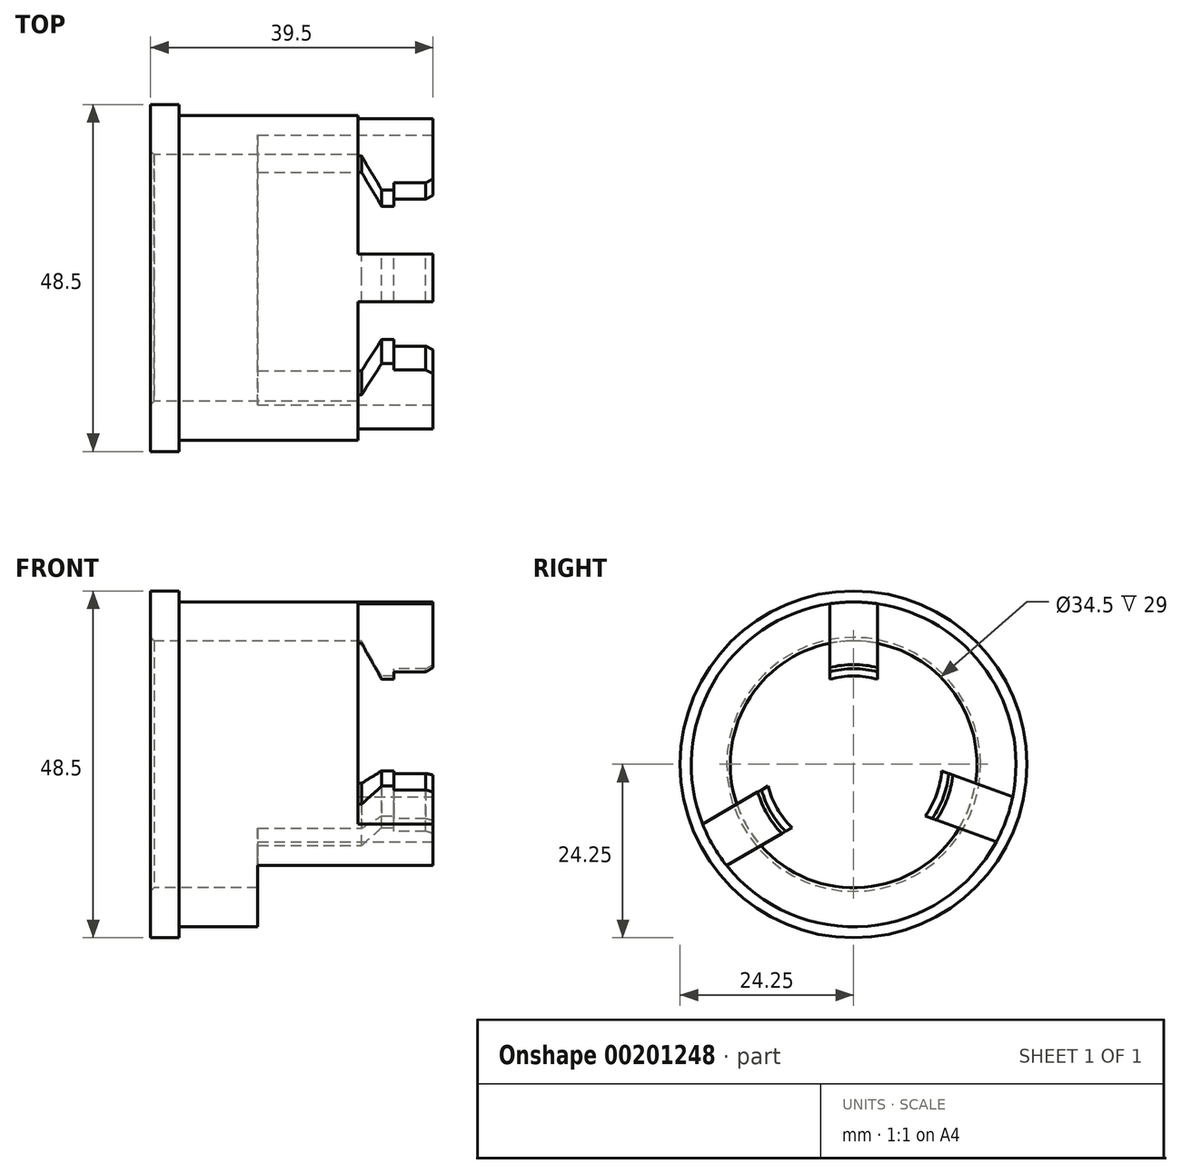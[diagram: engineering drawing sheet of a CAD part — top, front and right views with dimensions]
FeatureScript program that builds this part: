
annotation { "Feature Type Name" : "Feature", "Feature Type Description" : "" }
export const myFeature = defineFeature(function(context is Context, id is Id, definition is map)
    precondition{}
    {
        {
            var Q0;
            Q0=qCreatedBy(makeId("Front.planeOp"),FACE);
            var sketch = newSketch(context, id + "F0", { "sketchPlane" : qUnion([Q0])});
            skLineSegment(sketch, "E0", {"start": v(-7.14, 0) * mm, "end": v(50.19, 0) * mm, "construction": true});
            skLineSegment(sketch, "E1", {"start": v(0, 17.75) * mm, "end": v(0, 24.25) * mm});
            skLineSegment(sketch, "E2", {"start": v(0, 24.25) * mm, "end": v(4, 24.25) * mm});
            skLineSegment(sketch, "E3", {"start": v(4, 24.25) * mm, "end": v(4, 22.7) * mm});
            skLineSegment(sketch, "E4", {"start": v(4, 22.7) * mm, "end": v(39.5, 22.7) * mm});
            skLineSegment(sketch, "E5", {"start": v(39.5, 22.7) * mm, "end": v(39.5, 13.94) * mm});
            skLineSegment(sketch, "E6", {"start": v(39.5, 13.94) * mm, "end": v(38.5, 13.36) * mm});
            skLineSegment(sketch, "E7", {"start": v(38.5, 13.36) * mm, "end": v(34, 13.36) * mm});
            skLineSegment(sketch, "E8", {"start": v(34, 13.36) * mm, "end": v(34, 12.35) * mm});
            skLineSegment(sketch, "E9", {"start": v(34, 12.35) * mm, "end": v(32.33, 12.35) * mm});
            skLineSegment(sketch, "E10", {"start": v(32.33, 12.35) * mm, "end": v(29.5, 17.25) * mm});
            skLineSegment(sketch, "E11", {"start": v(29.5, 17.25) * mm, "end": v(0.5, 17.25) * mm});
            skLineSegment(sketch, "E12", {"start": v(0, 17.75) * mm, "end": v(0.5, 17.25) * mm});
            skSolve(sketch);
        }
        {
            var Q0;
            Q0=makeQuery(id+"F0.imprint","IMPRINT",FACE,{"disambiguationData":[TD([[makeQuery(id+"F0.imprint","IMPRINT",EDGE,{"derivedFrom":sQuery(id+"F0.wireOp",EDGE,"E1")}),-1.0]])]});
            var Q1;
            Q1=sQuery(id+"F0.wireOp",EDGE,"E0");
            revolve(context, id + "F1", {"entities" : qUnion([Q0]), "axis" : qUnion([Q1]), "revolveType" : RevolveType.FULL});
        }
        {
            var Q0;
            Q0=makeQuery(id+"F1.opRevolve","SWEPT_FACE",FACE,{"disambiguationData":[OSD([sQuery(id+"F0.wireOp",EDGE,"E5")])]});
            var sketch = newSketch(context, id + "F2", { "sketchPlane" : qUnion([Q0])});
            skLineSegment(sketch, "E13", {"start": v(0, 25.1) * mm, "end": v(0, -24.92) * mm, "construction": true});
            skLineSegment(sketch, "E14", {"start": v(-25.58, 0) * mm, "end": v(25.16, 0) * mm, "construction": true});
            skLineSegment(sketch, "E15", {"start": v(-3.35, 22.45) * mm, "end": v(-3.35, 11.89) * mm});
            skLineSegment(sketch, "E16", {"start": v(3.35, 22.45) * mm, "end": v(3.35, 11.89) * mm});
            skLineSegment(sketch, "E17", {"start": v(12.32, -0.92) * mm, "end": v(22.24, -4.53) * mm});
            skLineSegment(sketch, "E18", {"start": v(13.1, -4.77) * mm, "end": v(21.33, -7.76) * mm, "construction": true});
            skLineSegment(sketch, "E19", {"start": v(10.02, -7.21) * mm, "end": v(19.95, -10.83) * mm});
            skLineSegment(sketch, "E20", {"start": v(-19.66, -11.35) * mm, "end": v(-12.07, -6.97) * mm, "construction": true});
            skLineSegment(sketch, "E21", {"start": v(-21.12, -8.32) * mm, "end": v(-11.97, -3.04) * mm});
            skLineSegment(sketch, "E22", {"start": v(-17.77, -14.13) * mm, "end": v(-8.62, -8.84) * mm});
            skCircle(sketch, "E23.0", {"center": v(0, 0) * mm, "radius": 13.36 * mm});
            skCircle(sketch, "E24.0", {"center": v(0, 0) * mm, "radius": 12.35 * mm});
            skArc(sketch, "E25", {"start": v(-3.35, 16.92) * mm, "mid": v(-14.94, 8.62) * mm, "end": v(-16.33, -5.56) * mm});
            skArc(sketch, "E26.trimOffspring", {"start": v(17.05, -2.64) * mm, "mid": v(14.13, 9.9) * mm, "end": v(3.35, 16.92) * mm});
            skArc(sketch, "E27.trimOffspring", {"start": v(-12.98, -11.36) * mm, "mid": v(1.5, -17.18) * mm, "end": v(14.76, -8.94) * mm});
            skSolve(sketch);
        }
        {
            var Q0;
            {var subQ3=sQuery(id+"F2.wireOp",EDGE,"E25");Q0=makeQuery(id+"F2.imprint","IMPRINT",FACE,{"disambiguationData":[TD([[makeQuery(id+"F2.imprint","IMPRINT",EDGE,{"derivedFrom":subQ3}),-1.0]])]});}
            var Q1;
            {var subQ3=sQuery(id+"F2.wireOp",EDGE,"E26.trimOffspring");Q1=makeQuery(id+"F2.imprint","IMPRINT",FACE,{"disambiguationData":[TD([[makeQuery(id+"F2.imprint","IMPRINT",EDGE,{"derivedFrom":subQ3}),-1.0]])]});}
            extrude(context, id + "F3", {"entities" : qUnion([Q0, Q1]), "operationType" : NewBodyOperationType.REMOVE, "oppositeDirection" : true, "depth" : 10.5 * mm});
        }
        {
            var Q0;
            {var subQ0=sQuery(id+"F2.wireOp",EDGE,"E25");Q0=makeQuery(id+"F2.imprint","IMPRINT",FACE,{"disambiguationData":[TD([[makeQuery(id+"F2.imprint","IMPRINT",EDGE,{"derivedFrom":subQ0}),1.0]])]});}
            var Q1;
            {var subQ0=sQuery(id+"F2.wireOp",EDGE,"E26.trimOffspring");Q1=makeQuery(id+"F2.imprint","IMPRINT",FACE,{"disambiguationData":[TD([[makeQuery(id+"F2.imprint","IMPRINT",EDGE,{"derivedFrom":subQ0}),1.0]])]});}
            var Q2;
            {var subQ0=sQuery(id+"F2.wireOp",EDGE,"E24.0");var subQ1=sQuery(id+"F2.wireOp",EDGE,"E15");var subQ2=makeQuery(id+"F2.imprint","INTERSECT",VERTEX,{"derivedFrom":[subQ1,subQ0]});Q2=makeQuery(id+"F2.imprint","IMPRINT",FACE,{"disambiguationData":[TD([[makeQuery(id+"F2.imprint","IMPRINT",EDGE,{"disambiguationData":[TD([[subQ2,1.0]])],"derivedFrom":subQ1}),-1.0]])]});}
            var Q3;
            {var subQ0=sQuery(id+"F2.wireOp",EDGE,"E23.0");var subQ1=sQuery(id+"F2.wireOp",EDGE,"E15");var subQ2=makeQuery(id+"F2.imprint","INTERSECT",VERTEX,{"derivedFrom":[subQ1,subQ0]});Q3=makeQuery(id+"F2.imprint","IMPRINT",FACE,{"disambiguationData":[TD([[makeQuery(id+"F2.imprint","IMPRINT",EDGE,{"disambiguationData":[TD([[subQ2,-1.0]])],"derivedFrom":subQ0}),-1.0]])]});}
            var Q4;
            {var subQ0=sQuery(id+"F2.wireOp",EDGE,"E24.0");var subQ1=sQuery(id+"F2.wireOp",EDGE,"E16");var subQ2=makeQuery(id+"F2.imprint","INTERSECT",VERTEX,{"derivedFrom":[subQ1,subQ0]});Q4=makeQuery(id+"F2.imprint","IMPRINT",FACE,{"disambiguationData":[TD([[makeQuery(id+"F2.imprint","IMPRINT",EDGE,{"disambiguationData":[TD([[subQ2,1.0]])],"derivedFrom":subQ1}),1.0]])]});}
            var Q5;
            {var subQ0=sQuery(id+"F2.wireOp",EDGE,"E23.0");var subQ1=sQuery(id+"F2.wireOp",EDGE,"E16");var subQ2=makeQuery(id+"F2.imprint","INTERSECT",VERTEX,{"derivedFrom":[subQ1,subQ0]});Q5=makeQuery(id+"F2.imprint","IMPRINT",FACE,{"disambiguationData":[TD([[makeQuery(id+"F2.imprint","IMPRINT",EDGE,{"disambiguationData":[TD([[subQ2,1.0]])],"derivedFrom":subQ0}),-1.0]])]});}
            extrude(context, id + "F4", {"entities" : qUnion([Q0, Q1, Q2, Q3, Q4, Q5]), "operationType" : NewBodyOperationType.REMOVE, "endBound" : BoundingType.THROUGH_ALL, "oppositeDirection" : true, "depth" : 25 * mm});
        }
        {
            var Q0;
            {var subQ3=sQuery(id+"F2.wireOp",EDGE,"E27.trimOffspring");Q0=makeQuery(id+"F2.imprint","IMPRINT",FACE,{"disambiguationData":[TD([[makeQuery(id+"F2.imprint","IMPRINT",EDGE,{"derivedFrom":subQ3}),-1.0]])]});}
            extrude(context, id + "F5", {"entities" : qUnion([Q0]), "operationType" : NewBodyOperationType.REMOVE, "oppositeDirection" : true, "depth" : 24.5 * mm});
        }
        {
            var Q0;
            {var subQ0=sQuery(id+"F2.wireOp",EDGE,"E27.trimOffspring");Q0=makeQuery(id+"F2.imprint","IMPRINT",FACE,{"disambiguationData":[TD([[makeQuery(id+"F2.imprint","IMPRINT",EDGE,{"derivedFrom":subQ0}),1.0]])]});}
            var Q1;
            {var subQ0=sQuery(id+"F2.wireOp",EDGE,"E24.0");var subQ1=sQuery(id+"F2.wireOp",EDGE,"E19");var subQ2=makeQuery(id+"F2.imprint","INTERSECT",VERTEX,{"derivedFrom":[subQ1,subQ0]});Q1=makeQuery(id+"F2.imprint","IMPRINT",FACE,{"disambiguationData":[TD([[makeQuery(id+"F2.imprint","IMPRINT",EDGE,{"disambiguationData":[TD([[subQ2,-1.0]])],"derivedFrom":subQ1}),-1.0]])]});}
            var Q2;
            {var subQ0=sQuery(id+"F2.wireOp",EDGE,"E23.0");var subQ1=sQuery(id+"F2.wireOp",EDGE,"E19");var subQ2=makeQuery(id+"F2.imprint","INTERSECT",VERTEX,{"derivedFrom":[subQ1,subQ0]});Q2=makeQuery(id+"F2.imprint","IMPRINT",FACE,{"disambiguationData":[TD([[makeQuery(id+"F2.imprint","IMPRINT",EDGE,{"disambiguationData":[TD([[subQ2,1.0]])],"derivedFrom":subQ0}),-1.0]])]});}
            extrude(context, id + "F6", {"entities" : qUnion([Q0, Q1, Q2]), "operationType" : NewBodyOperationType.REMOVE, "endBound" : BoundingType.THROUGH_ALL, "oppositeDirection" : true, "depth" : 25 * mm});
        }
    });
